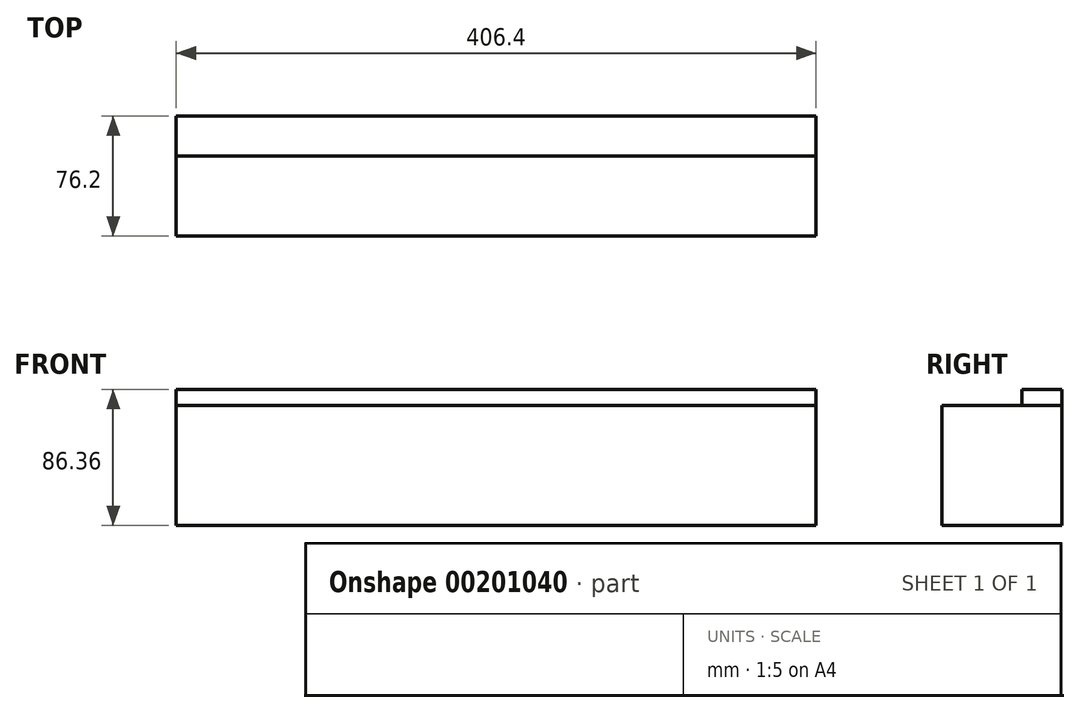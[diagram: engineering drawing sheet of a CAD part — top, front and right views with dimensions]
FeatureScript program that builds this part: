
annotation { "Feature Type Name" : "Feature", "Feature Type Description" : "" }
export const myFeature = defineFeature(function(context is Context, id is Id, definition is map)
    precondition{}
    {
        {
            var Q0;
            Q0=qCreatedBy(makeId("Right.planeOp"),FACE);
            var sketch = newSketch(context, id + "F0", { "sketchPlane" : qUnion([Q0])});
            skLineSegment(sketch, "E0.bottom", {"start": v(38.1, -38.1) * mm, "end": v(-38.1, -38.1) * mm});
            skLineSegment(sketch, "E0.top", {"start": v(38.1, 38.1) * mm, "end": v(-38.1, 38.1) * mm});
            skLineSegment(sketch, "E0.left", {"start": v(38.1, -38.1) * mm, "end": v(38.1, 38.1) * mm});
            skLineSegment(sketch, "E0.right", {"start": v(-38.1, -38.1) * mm, "end": v(-38.1, 38.1) * mm});
            skPoint(sketch, "E0.middle", {"position": v(0, 0) * mm});
            skSolve(sketch);
        }
        {
            var Q0;
            Q0 = qSketchRegion(id + "F0", true);
            extrude(context, id + "F1", {"entities" : qUnion([Q0]), "oppositeDirection" : true, "depth" : 203.2 * mm, "hasSecondDirection" : true, "secondDirectionOppositeDirection" : false, "secondDirectionDepth" : 203.2 * mm});
        }
        {
            var Q0;
            Q0=qCreatedBy(makeId("Right.planeOp"),FACE);
            var sketch = newSketch(context, id + "F2", { "sketchPlane" : qUnion([Q0])});
            skLineSegment(sketch, "E1.bottom", {"start": v(38.1, 38.1) * mm, "end": v(12.7, 38.1) * mm});
            skLineSegment(sketch, "E1.top", {"start": v(38.1, 48.26) * mm, "end": v(12.7, 48.26) * mm});
            skLineSegment(sketch, "E1.left", {"start": v(38.1, 38.1) * mm, "end": v(38.1, 48.26) * mm});
            skLineSegment(sketch, "E1.right", {"start": v(12.7, 38.1) * mm, "end": v(12.7, 48.26) * mm});
            skSolve(sketch);
        }
        {
            var Q0;
            Q0 = qSketchRegion(id + "F2", true);
            extrude(context, id + "F3", {"entities" : qUnion([Q0]), "depth" : 203.2 * mm, "hasSecondDirection" : true, "secondDirectionOppositeDirection" : true, "secondDirectionDepth" : 203.2 * mm});
        }
    });
